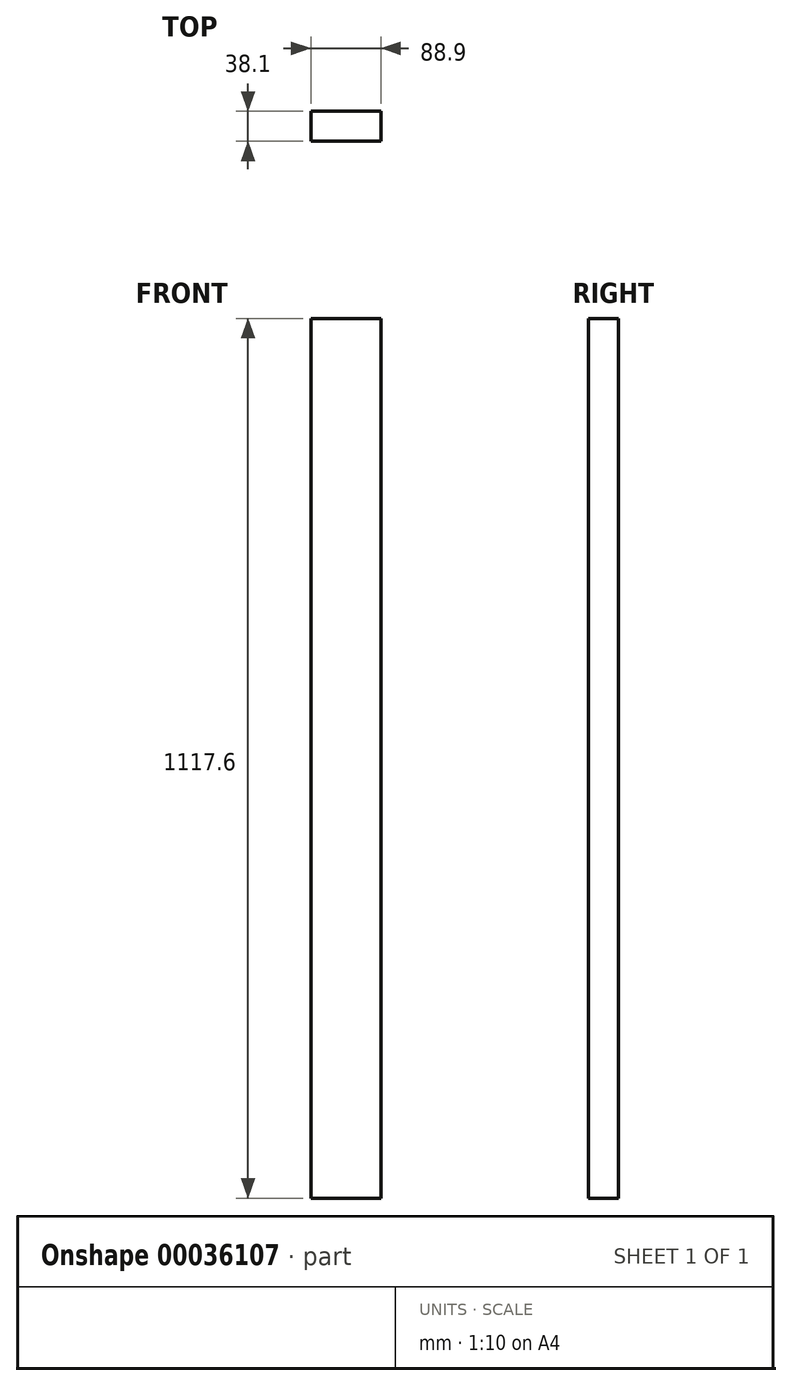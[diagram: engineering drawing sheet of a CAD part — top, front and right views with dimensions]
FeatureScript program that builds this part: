
annotation { "Feature Type Name" : "Feature", "Feature Type Description" : "" }
export const myFeature = defineFeature(function(context is Context, id is Id, definition is map)
    precondition{}
    {
        {
            var Q0;
            Q0=qCreatedBy(makeId("Front.planeOp"),FACE);
            var sketch = newSketch(context, id + "F0", { "sketchPlane" : qUnion([Q0])});
            skLineSegment(sketch, "E0.bottom", {"start": v(0, 0) * mm, "end": v(88.9, 0) * mm});
            skLineSegment(sketch, "E0.top", {"start": v(0, 1117.6) * mm, "end": v(88.9, 1117.6) * mm});
            skLineSegment(sketch, "E0.left", {"start": v(0, 0) * mm, "end": v(0, 1117.6) * mm});
            skLineSegment(sketch, "E0.right", {"start": v(88.9, 0) * mm, "end": v(88.9, 1117.6) * mm});
            skSolve(sketch);
        }
        {
            var Q0;
            Q0=makeQuery(id+"F0.imprint","IMPRINT",FACE,{"disambiguationData":[TD([[makeQuery(id+"F0.imprint","IMPRINT",EDGE,{"derivedFrom":sQuery(id+"F0.wireOp",EDGE,"E0.bottom")}),1.0]])]});
            extrude(context, id + "F1", {"entities" : qUnion([Q0]), "depth" : 38.1 * mm});
        }
    });
